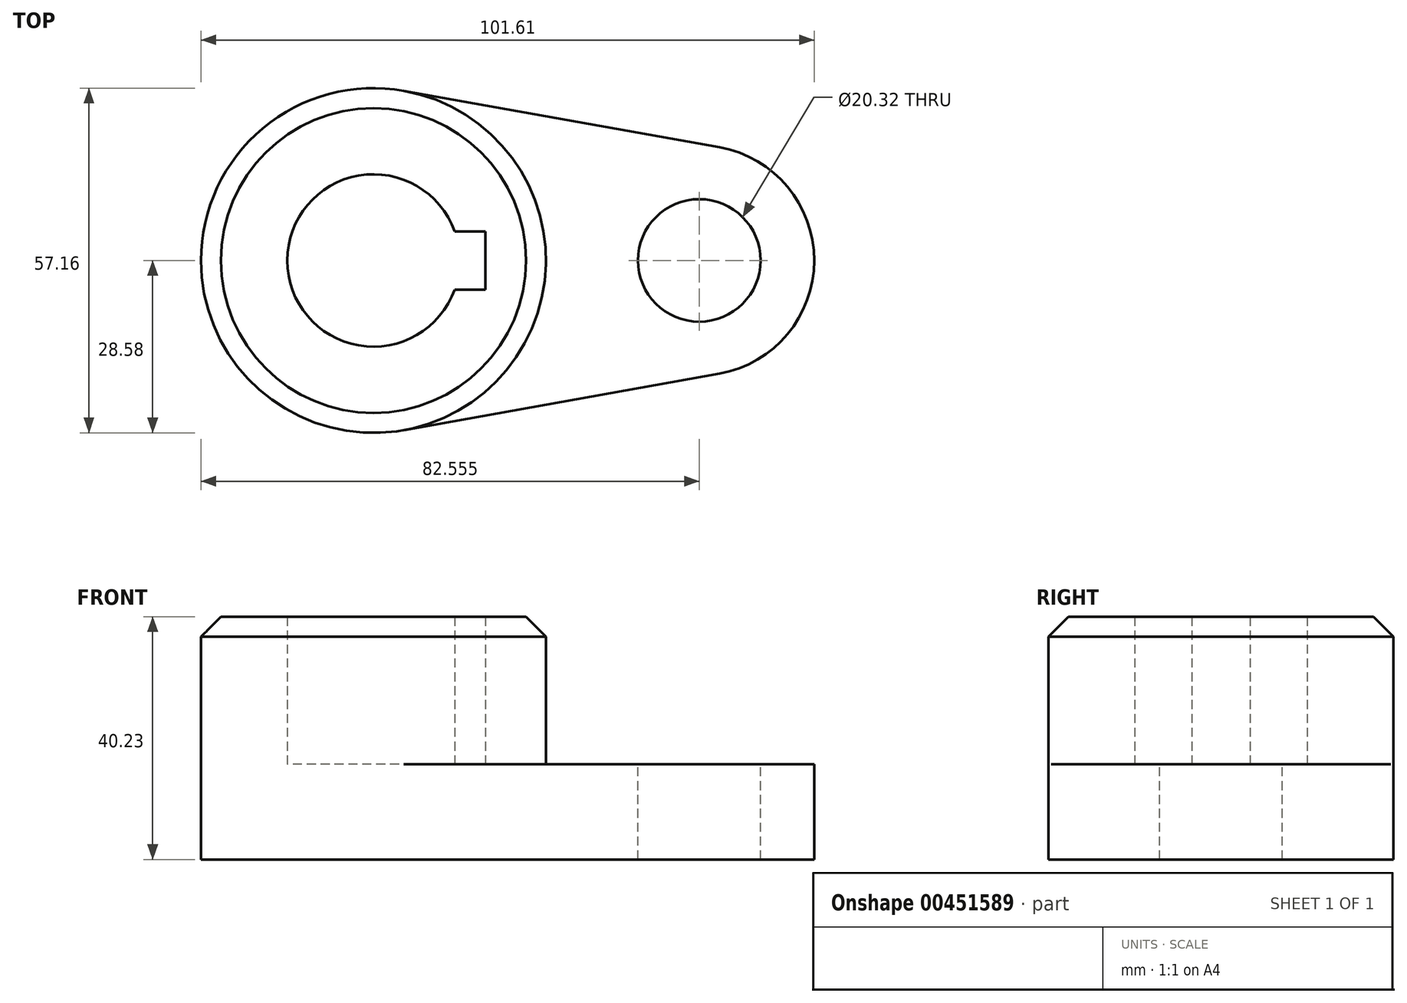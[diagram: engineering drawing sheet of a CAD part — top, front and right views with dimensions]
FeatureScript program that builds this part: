
annotation { "Feature Type Name" : "Feature", "Feature Type Description" : "" }
export const myFeature = defineFeature(function(context is Context, id is Id, definition is map)
    precondition{}
    {
        {
            var Q0;
            Q0=qCreatedBy(makeId("Top.planeOp"),FACE);
            var sketch = newSketch(context, id + "F0", { "sketchPlane" : qUnion([Q0])});
            skArc(sketch, "E0", {"start": v(5.04, 28.13) * mm, "mid": v(-28.57, 0) * mm, "end": v(5.04, -28.13) * mm});
            skArc(sketch, "E1", {"start": v(57.34, -18.75) * mm, "mid": v(73.03, 0) * mm, "end": v(57.34, 18.75) * mm});
            skLineSegment(sketch, "E2", {"start": v(5.04, -28.13) * mm, "end": v(57.34, -18.75) * mm});
            skLineSegment(sketch, "E3", {"start": v(5.04, 28.13) * mm, "end": v(57.34, 18.75) * mm});
            skCircle(sketch, "E4", {"center": v(53.98, 0) * mm, "radius": 10.16 * mm});
            skSolve(sketch);
        }
        {
            var Q0;
            Q0=makeQuery(id+"F0.imprint","IMPRINT",FACE,{"disambiguationData":[TD([[makeQuery(id+"F0.imprint","IMPRINT",EDGE,{"derivedFrom":sQuery(id+"F0.wireOp",EDGE,"E0")}),1.0]])]});
            extrude(context, id + "F1", {"entities" : qUnion([Q0]), "oppositeDirection" : true, "depth" : 15.77 * mm});
        }
        {
            var Q0;
            Q0=makeQuery(id+"F1.opExtrude","CAP_FACE",FACE,{"disambiguationData":[OSD([sQuery(id+"F0.wireOp",EDGE,"E0"),sQuery(id+"F0.wireOp",EDGE,"E1"),sQuery(id+"F0.wireOp",EDGE,"E2"),sQuery(id+"F0.wireOp",EDGE,"E3"),sQuery(id+"F0.wireOp",EDGE,"E4")])],"isStart":false});
            var sketch = newSketch(context, id + "F2", { "sketchPlane" : qUnion([Q0])});
            skArc(sketch, "E5", {"start": v(13.45, 4.83) * mm, "mid": v(-14.29, 0) * mm, "end": v(13.45, -4.83) * mm});
            skLineSegment(sketch, "E6", {"start": v(18.53, 4.83) * mm, "end": v(18.53, -4.83) * mm});
            skLineSegment(sketch, "E7", {"start": v(18.53, 4.83) * mm, "end": v(13.45, 4.83) * mm});
            skLineSegment(sketch, "E8", {"start": v(18.53, -4.83) * mm, "end": v(13.45, -4.83) * mm});
            skCircle(sketch, "E9", {"center": v(0, 0) * mm, "radius": 28.58 * mm});
            skSolve(sketch);
        }
        {
            var Q0;
            Q0=makeQuery(id+"F2.imprint","IMPRINT",FACE,{"disambiguationData":[TD([[makeQuery(id+"F2.imprint","IMPRINT",EDGE,{"derivedFrom":sQuery(id+"F2.wireOp",EDGE,"E5")}),-1.0]])]});
            extrude(context, id + "F3", {"entities" : qUnion([Q0]), "operationType" : NewBodyOperationType.ADD, "oppositeDirection" : true, "depth" : 40.23 * mm});
        }
        {
            var Q0;
            Q0=makeQuery(id+"F3.opExtrude","CAP_EDGE",EDGE,{"disambiguationData":[OSD([sQuery(id+"F2.wireOp",EDGE,"E9")])],"isStart":false});
            chamfer(context, id + "F4", {"entities" : qUnion([Q0]), "width" : 3.3 * mm, "tangentPropagation" : true});
        }
    });
